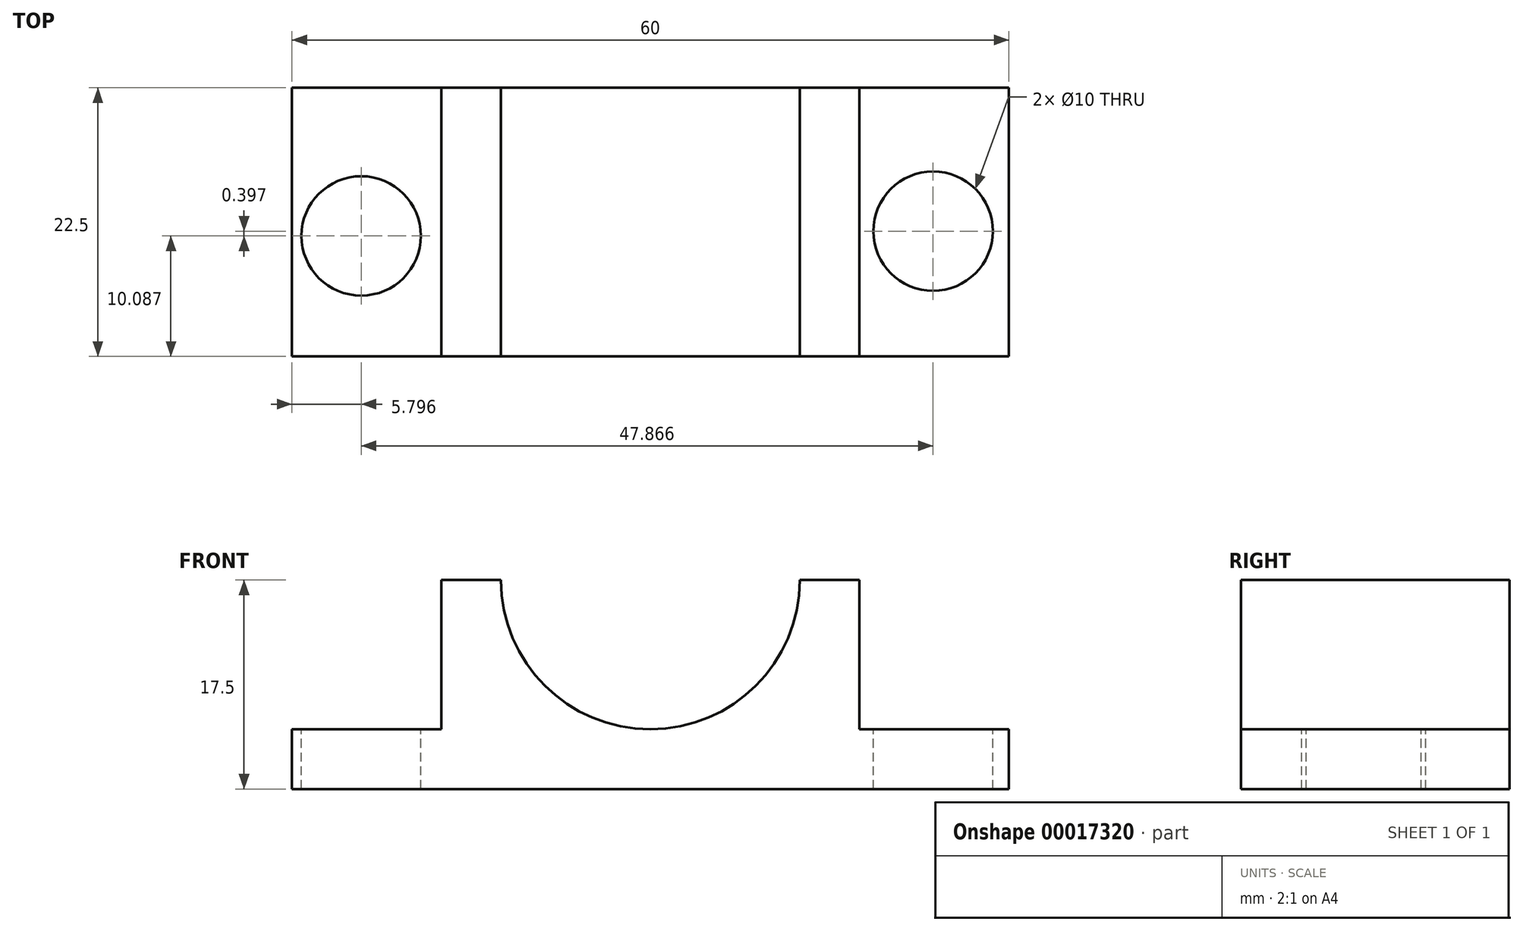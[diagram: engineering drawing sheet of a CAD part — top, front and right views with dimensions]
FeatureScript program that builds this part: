
annotation { "Feature Type Name" : "Feature", "Feature Type Description" : "" }
export const myFeature = defineFeature(function(context is Context, id is Id, definition is map)
    precondition{}
    {
        {
            var Q0;
            Q0=qCreatedBy(makeId("Front.planeOp"),FACE);
            var sketch = newSketch(context, id + "F0", { "sketchPlane" : qUnion([Q0])});
            skLineSegment(sketch, "E0", {"start": v(-32.82, 12.5) * mm, "end": v(-32.82, 0) * mm});
            skLineSegment(sketch, "E1", {"start": v(-32.82, 0) * mm, "end": v(-45.32, 0) * mm});
            skLineSegment(sketch, "E2", {"start": v(-45.32, 0) * mm, "end": v(-45.32, -5) * mm});
            skLineSegment(sketch, "E3", {"start": v(2.18, 12.5) * mm, "end": v(2.18, 0) * mm});
            skLineSegment(sketch, "E4", {"start": v(2.18, 0) * mm, "end": v(14.68, 0) * mm});
            skLineSegment(sketch, "E5", {"start": v(14.68, 0) * mm, "end": v(14.68, -5) * mm});
            skLineSegment(sketch, "E6", {"start": v(-45.32, -5) * mm, "end": v(14.68, -5) * mm});
            skArc(sketch, "E7", {"start": v(-27.82, 12.5) * mm, "mid": v(-15.32, 0) * mm, "end": v(-2.82, 12.5) * mm});
            skLineSegment(sketch, "E8", {"start": v(-32.82, 12.5) * mm, "end": v(-27.82, 12.5) * mm});
            skLineSegment(sketch, "E9", {"start": v(-2.82, 12.5) * mm, "end": v(2.18, 12.5) * mm});
            skSolve(sketch);
        }
        {
            var Q0;
            Q0=makeQuery(id+"F0.imprint","IMPRINT",FACE,{"disambiguationData":[TD([[makeQuery(id+"F0.imprint","IMPRINT",EDGE,{"derivedFrom":sQuery(id+"F0.wireOp",EDGE,"E0")}),1.0]])]});
            extrude(context, id + "F1", {"entities" : qUnion([Q0]), "depth" : 22.5 * mm});
        }
        {
            var Q0;
            Q0=makeQuery(id+"F1.opExtrude","SWEPT_FACE",FACE,{"disambiguationData":[OSD([sQuery(id+"F0.wireOp",EDGE,"E1")])]});
            var sketch = newSketch(context, id + "F2", { "sketchPlane" : qUnion([Q0])});
            skCircle(sketch, "E10", {"center": v(8.34, -12.02) * mm, "radius": 5 * mm});
            skSolve(sketch);
        }
        {
            var Q0;
            Q0=makeQuery(id+"F2.imprint","IMPRINT",FACE,{"disambiguationData":[TD([[makeQuery(id+"F2.imprint","IMPRINT",EDGE,{"derivedFrom":sQuery(id+"F2.wireOp",EDGE,"E10")}),1.0]])]});
            extrude(context, id + "F3", {"entities" : qUnion([Q0]), "operationType" : NewBodyOperationType.REMOVE, "endBound" : BoundingType.THROUGH_ALL, "oppositeDirection" : true, "depth" : 25 * mm});
        }
        {
            var Q0;
            Q0=makeQuery(id+"F1.opExtrude","SWEPT_FACE",FACE,{"disambiguationData":[OSD([sQuery(id+"F0.wireOp",EDGE,"E1")])]});
            var sketch = newSketch(context, id + "F4", { "sketchPlane" : qUnion([Q0])});
            skCircle(sketch, "E11", {"center": v(-39.52, -12.41) * mm, "radius": 5 * mm});
            skSolve(sketch);
        }
        {
            var Q0;
            Q0=makeQuery(id+"F4.imprint","IMPRINT",FACE,{"disambiguationData":[TD([[makeQuery(id+"F4.imprint","IMPRINT",EDGE,{"derivedFrom":sQuery(id+"F4.wireOp",EDGE,"E11")}),1.0]])]});
            extrude(context, id + "F5", {"entities" : qUnion([Q0]), "operationType" : NewBodyOperationType.REMOVE, "endBound" : BoundingType.THROUGH_ALL, "oppositeDirection" : true, "depth" : 25 * mm});
        }
    });
